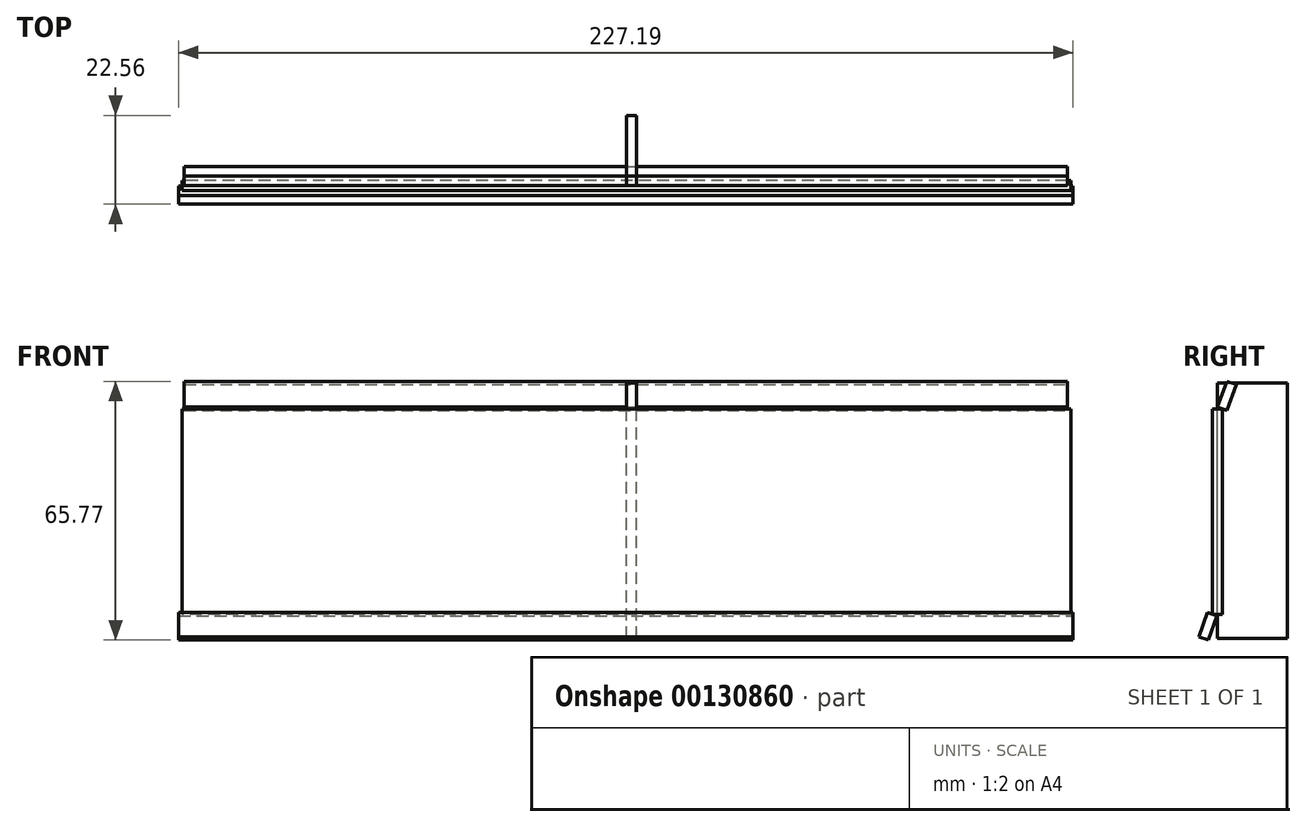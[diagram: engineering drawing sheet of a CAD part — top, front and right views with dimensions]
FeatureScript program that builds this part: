
annotation { "Feature Type Name" : "Feature", "Feature Type Description" : "" }
export const myFeature = defineFeature(function(context is Context, id is Id, definition is map)
    precondition{}
    {
        {
            var Q0;
            Q0=qCreatedBy(makeId("Front.planeOp"),FACE);
            var sketch = newSketch(context, id + "F0", { "sketchPlane" : qUnion([Q0])});
            skLineSegment(sketch, "E0.bottom", {"start": v(112.89, -26.1) * mm, "end": v(-112.89, -26.1) * mm});
            skLineSegment(sketch, "E0.top", {"start": v(112.89, 26.1) * mm, "end": v(-112.89, 26.1) * mm});
            skLineSegment(sketch, "E0.left", {"start": v(112.89, -26.1) * mm, "end": v(112.89, 26.1) * mm});
            skLineSegment(sketch, "E0.right", {"start": v(-112.89, -26.1) * mm, "end": v(-112.89, 26.1) * mm});
            skPoint(sketch, "E0.middle", {"position": v(0, 0) * mm});
            skSolve(sketch);
        }
        {
            var Q0;
            Q0 = qSketchRegion(id + "F0", true);
            extrude(context, id + "F1", {"entities" : qUnion([Q0]), "endBound" : BoundingType.SYMMETRIC, "depth" : 2.54 * mm});
        }
        {
            var Q0;
            Q0=makeQuery(id+"F1.opExtrude","CAP_EDGE",EDGE,{"disambiguationData":[OSD([sQuery(id+"F0.wireOp",EDGE,"E0.top")])],"isStart":true});
            cPlane(context, id + "F2", {"entities" : qUnion([Q0]), "cplaneType" : CPlaneType.LINE_ANGLE, "offset" : 25.4 * mm, "angle" : 20 * degree, "width" : 152.4 * mm, "height" : 152.4 * mm});
        }
        {
            var Q0;
            Q0=qCreatedBy(id+"F2.planeOp",FACE);
            var sketch = newSketch(context, id + "F3", { "sketchPlane" : qUnion([Q0])});
            skLineSegment(sketch, "E1.bottom", {"start": v(-112.41, 24.96) * mm, "end": v(111.94, 24.96) * mm});
            skLineSegment(sketch, "E1.top", {"start": v(-112.41, 31.97) * mm, "end": v(111.94, 31.97) * mm});
            skLineSegment(sketch, "E1.left", {"start": v(-112.41, 24.96) * mm, "end": v(-112.41, 31.97) * mm});
            skLineSegment(sketch, "E1.right", {"start": v(111.94, 24.96) * mm, "end": v(111.94, 31.97) * mm});
            skSolve(sketch);
        }
        {
            var Q0;
            Q0=makeQuery(id+"F3.imprint","IMPRINT",FACE,{"disambiguationData":[TD([[makeQuery(id+"F3.imprint","IMPRINT",EDGE,{"derivedFrom":sQuery(id+"F3.wireOp",EDGE,"E1.bottom")}),1.0]])]});
            extrude(context, id + "F4", {"entities" : qUnion([Q0]), "endBound" : BoundingType.SYMMETRIC, "depth" : 2.54 * mm});
        }
        {
            var Q0;
            Q0=makeQuery(id+"F1.opExtrude","CAP_EDGE",EDGE,{"disambiguationData":[OSD([sQuery(id+"F0.wireOp",EDGE,"E0.bottom")])],"isStart":false});
            cPlane(context, id + "F5", {"entities" : qUnion([Q0]), "cplaneType" : CPlaneType.LINE_ANGLE, "offset" : 25.4 * mm, "angle" : 20 * degree, "width" : 152.4 * mm, "height" : 152.4 * mm});
        }
        {
            var Q0;
            Q0=qCreatedBy(id+"F5.planeOp",FACE);
            var sketch = newSketch(context, id + "F6", { "sketchPlane" : qUnion([Q0])});
            skLineSegment(sketch, "E2.bottom", {"start": v(-113.83, -24.96) * mm, "end": v(113.36, -24.96) * mm});
            skLineSegment(sketch, "E2.top", {"start": v(-113.83, -31.47) * mm, "end": v(113.36, -31.47) * mm});
            skLineSegment(sketch, "E2.left", {"start": v(-113.83, -24.96) * mm, "end": v(-113.83, -31.47) * mm});
            skLineSegment(sketch, "E2.right", {"start": v(113.36, -24.96) * mm, "end": v(113.36, -31.47) * mm});
            skSolve(sketch);
        }
        {
            var Q0;
            Q0 = qSketchRegion(id + "F6", true);
            extrude(context, id + "F7", {"entities" : qUnion([Q0]), "endBound" : BoundingType.SYMMETRIC, "depth" : 2.54 * mm});
        }
        {
            var Q0;
            Q0=qCreatedBy(makeId("Right.planeOp"),FACE);
            var sketch = newSketch(context, id + "F8", { "sketchPlane" : qUnion([Q0])});
            skLineSegment(sketch, "E3.bottom", {"start": v(0, -32.22) * mm, "end": v(17.87, -32.22) * mm});
            skLineSegment(sketch, "E3.top", {"start": v(0, 32.69) * mm, "end": v(17.87, 32.69) * mm});
            skLineSegment(sketch, "E3.left", {"start": v(0, -32.22) * mm, "end": v(0, 32.69) * mm});
            skLineSegment(sketch, "E3.right", {"start": v(17.87, -32.22) * mm, "end": v(17.87, 32.69) * mm});
            skSolve(sketch);
        }
        {
            var Q0;
            Q0 = qSketchRegion(id + "F8", true);
            extrude(context, id + "F9", {"entities" : qUnion([Q0]), "depth" : 2.54 * mm});
        }
    });
